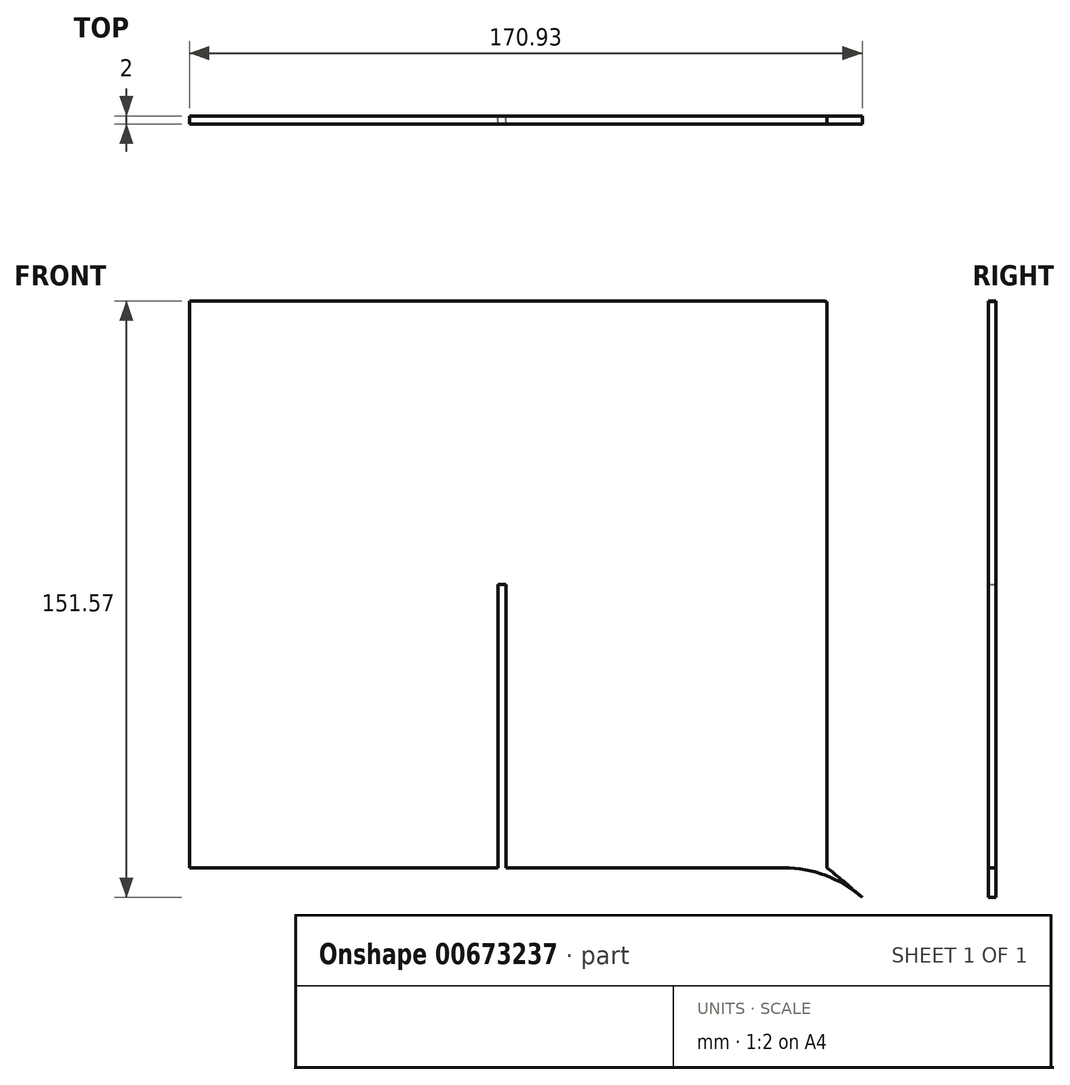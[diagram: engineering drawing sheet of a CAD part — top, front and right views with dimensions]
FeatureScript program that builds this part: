
annotation { "Feature Type Name" : "Feature", "Feature Type Description" : "" }
export const myFeature = defineFeature(function(context is Context, id is Id, definition is map)
    precondition{}
    {
        {
            var Q0;
            Q0=qCreatedBy(makeId("Front.planeOp"),FACE);
            var sketch = newSketch(context, id + "F0", { "sketchPlane" : qUnion([Q0])});
            skLineSegment(sketch, "E0.bottom", {"start": v(-81, 72) * mm, "end": v(78.58, 72) * mm});
            skLineSegment(sketch, "E0.top", {"start": v(-81, -72) * mm, "end": v(-2.58, -72) * mm});
            skLineSegment(sketch, "E0.left", {"start": v(-81, 72) * mm, "end": v(-81, -72) * mm});
            skLineSegment(sketch, "E0.right", {"start": v(81, 72) * mm, "end": v(81, -72) * mm});
            skPoint(sketch, "E0.middle", {"position": v(0, 0) * mm});
            skLineSegment(sketch, "E1", {"start": v(212.05, 0.82) * mm, "end": v(246.1, -87.87) * mm});
            skLineSegment(sketch, "E2", {"start": v(81, -72) * mm, "end": v(240, -72) * mm, "construction": true});
            skLineSegment(sketch, "E3", {"start": v(212.05, 0.82) * mm, "end": v(188.7, -8.14) * mm});
            skLineSegment(sketch, "E4", {"start": v(246.1, -87.87) * mm, "end": v(231.83, -93.35) * mm});
            skFitSpline(sketch, "E5", {"points": [v(81, -72) * mm, v(112.66, -100.64) * mm, v(153.75, -114.8) * mm, v(218.08, -98.62) * mm], "startDerivative": vector(199.96, -162.47) * mm, "endDerivative": vector(219.31, 82.89) * mm});
            skFitSpline(sketch, "E6", {"points": [v(81, 72) * mm, v(122.8, 35.43) * mm, v(142.72, 4.45) * mm, v(188.7, -8.14) * mm], "startDerivative": vector(192.8, -42.78) * mm, "endDerivative": vector(158.98, 53.13) * mm});
            skArc(sketch, "E7.filletArc", {"start": v(83.88, 71.28) * mm, "mid": v(81.26, 71.82) * mm, "end": v(78.58, 72) * mm});
            skArc(sketch, "E8.filletArc", {"start": v(89.93, -79.57) * mm, "mid": v(80.67, -73.96) * mm, "end": v(70.01, -72) * mm});
            skLineSegment(sketch, "E9.top", {"start": v(-0.58, 0) * mm, "end": v(-2.58, 0) * mm});
            skLineSegment(sketch, "E9.left", {"start": v(-0.58, -72) * mm, "end": v(-0.58, 0) * mm});
            skLineSegment(sketch, "E9.right", {"start": v(-2.58, -72) * mm, "end": v(-2.58, 0) * mm});
            skLineSegment(sketch, "E10", {"start": v(231.83, -93.35) * mm, "end": v(214.8, -49) * mm});
            skLineSegment(sketch, "E11", {"start": v(214.8, -49) * mm, "end": v(212.94, -49.72) * mm});
            skLineSegment(sketch, "E12", {"start": v(212.94, -49.72) * mm, "end": v(229.96, -94.06) * mm});
            skLineSegment(sketch, "E13.trimOffspring", {"start": v(-0.58, -72) * mm, "end": v(70.01, -72) * mm});
            skLineSegment(sketch, "E14.trimOffspring", {"start": v(229.96, -94.06) * mm, "end": v(218.08, -98.62) * mm});
            skSolve(sketch);
        }
        {
            var Q0;
            {var subQ1=sQuery(id+"F0.wireOp",EDGE,"E0.bottom");Q0=makeQuery(id+"F0.imprint","IMPRINT",FACE,{"disambiguationData":[TD([[makeQuery(id+"F0.imprint","IMPRINT",EDGE,{"derivedFrom":subQ1}),-1.0]])]});}
            extrude(context, id + "F1", {"entities" : qUnion([Q0]), "endBound" : BoundingType.SYMMETRIC, "depth" : 2 * mm, "offsetDistance" : 25 * mm});
        }
    });
